# Revit family: AT-1-M_RFA
name_source: partatom
category: Aparatos sanitarios
units: mm (PartAtom-declared; Revit-internal decimal feet)

## family parameters
Compartido = Sí
Corte con vacíos al cargar = No
Cota de conector redondo = Diámetro de uso
Número OmniClass = 23.45.00.00
Punto de cálculo de habitación = No
Se basa en plano de trabajo = No
Siempre vertical = Sí
Tipo de pieza = Normal
Título OmniClass = Sanitary, Laundry, and Cleaning Equipment

## types (1)
- AT-1
    Comentarios de tipo = SANIVEX
    Data Sheet = http://www.helvex.com.mx
    Descripción = Plus Seat Elongated Front Toilet With Lid Open, Close Slow And Antibacterial, White
    Elevación por defecto = 0"
    Fabricante = HELVEX
    Features = Glossy Finish; Antibacterial Protection; Close Slow
    Instructive = http://www.helvex.com.mx
    Marfil = Marfil
    Modelo = AT-1
    Placement Height = 14.5"
    Polypropylene = Polypropylene
    Total Height = 2"
    Total Length = 19"
    Total Weight = 2.46 lb
    Total Width = 14"
    URL = http://www.helvex.com.mx

## geometry (parser evidence)
native form markers: Sweep x2
no freeform markers — native parametric forms only
